# Revit family: IS_Iom_A9112_BIM_NL
name_source: partatom
category: Plumbing Fixtures
revit_build: Autodesk Revit MEP 2016 (Build: 20161004_0715(x64)
units: mm (PartAtom-declared; Revit-internal decimal feet)

## family parameters
Always vertical = No
Cut with Voids When Loaded = No
OmniClass Number = 23.45.05.14.21.11
OmniClass Title = Bath/Shower Units
Part Type = Normal
Room Calculation Point = No
Round Connector Dimension = Use Diameter
Shared = No
Work Plane-Based = No

## types (1)
- A9112AA - IOM ZEEPBAKJE DRAADMODEL CHROOM
    Accesoires = www.idealstandardnederland.nl
    Afmetingen = 0
    Afwerking = Chroom
    Artikelnummer = A9112AA
    Artikelomschrijving = ISI_IOM_SoapDishes_A9112AA
    Artikelreferentie = IOM ZEEPBAKJE DRAADMODEL CHROOM
    Auteur = Ideal Standard
    BIMobject category = Accessories
    BOSUseNativeGeometries = 1
    Barcode = 4015413328012
    Beschrijvinggarantie = 4015413328012
    Brand url = www.idealstandardnederland.nl
    Breedte = 0
    BrutoGewicht = 0
    Cost = 0 $
    Description = IOM ZEEPBAKJE DRAADMODEL CHROOM
    Diepte = 0 mm  [stored 0 ft]
    EAN code = https://4015413328012
    Edition number = 1
    Eigenschappen = Zeepbak. Inclusief bevestigingsset. Makkelijk schoon te maken, functioneel design. Korf en houder van metaal. 2 geïntegreerde bevestigingspunten.
    Garantieonderdelen = 1
    Garantieunits = Jaar
    Hoogte = 0
    IFC Classification = Sanitary Terminal
    IfcExportAs = Ifc Sanitary Terminal Type
    Installatieinstructies = http://www.idealstandardnederland.nl
    Installation instructions = www.idealstandardnederland.nl
    Kleur = Chroom
    Lengte = 0 mm  [stored 0 ft]
    Manufacturer = www.idealstandardnederland.nl
    Manufacturer name = Ideal Standard
    Materiaal = Messing
    Merk = Ideal Standard
    Model = A9112AA
    NBS Reference Code = 35-75-82
    NBS Reference Description = Soap Dishes
    Nettogewicht = 0
    Nominal height = 48
    Nominal width = 197
    NominalHeight = 48 mm  [stored 0.15748 ft]
    NominalLength = 140 mm
    NominalWidth = 195 mm
    OmniClass Code = 23-31 25 00
    OmniClass Description = Toilet and Bath Specialties
    Product Guid = d419ac60-7071-4335-bc00-3e226bc88ae1
    Product SKU = A9112
    Product data url = https://bimobject.com
    Product family = IOM
    Product group = Accessories
    Product name = IOM Soap basket
    QR code = http://bimobject.com
    Revisie = 1
    Size = 48 x 140 x 195mm
    Technical description = www.idealstandardnederland.nl
    Telefoonnummer = 31 (0) 77 355 08 08
    Typeconnectie = Sanitair
    URL = www.idealstandardnederland.nl
    Uniclass 1.4 Code = L8246
    Uniclass 1.4 Description = Soap holders/dispensers
    Uniclass 2.0 Code = PR-35-75-82
    Uniclass 2.0 Description = Soap Dishes
    Uniclass 2015 Code = Pr_40_20_76_82
    Uniclass 2015 Name = Soap dishes
    Uniclass2015Beschrijving = Soap dishes
    Uniclass2015Referentie = Pr_40_20_76_82
    Uniclass2015Version = Products v1.1
    Versie = 1
    Vervangingskosten = 0
    Volumeunits = Liter
    Weight Net (Kg) = 0.45

note: [stored X ft] marks values corroborated as IEEE doubles in the binary element streams (Revit-internal decimal feet)

## geometry (parser evidence)
native form markers: Blend x4, Sweep x1
no freeform markers — native parametric forms only
